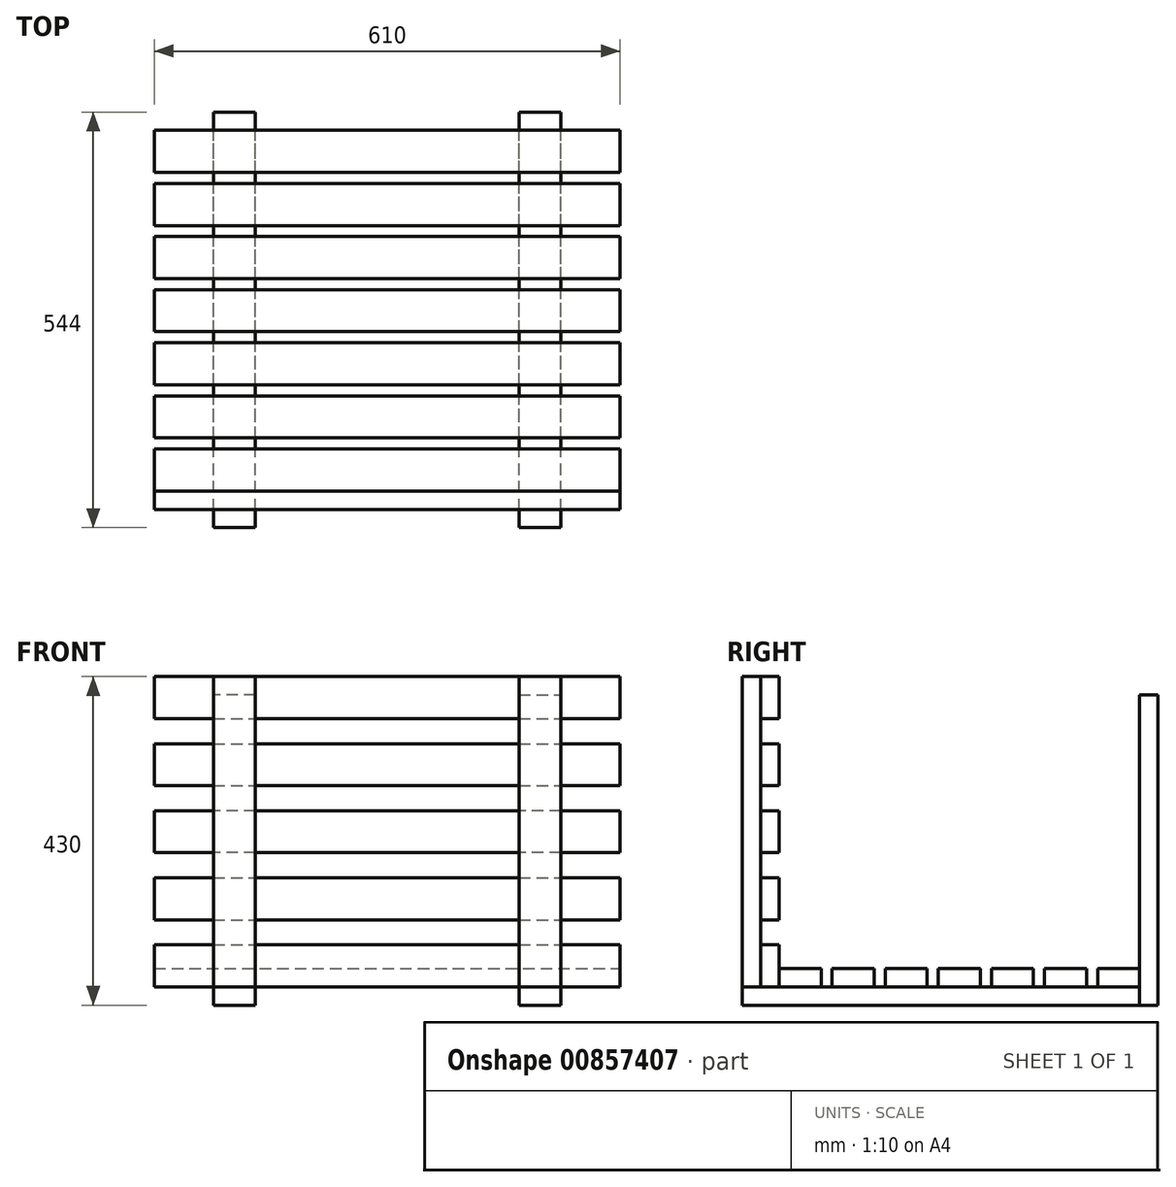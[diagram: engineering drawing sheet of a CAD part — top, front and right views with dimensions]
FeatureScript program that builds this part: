
annotation { "Feature Type Name" : "Feature", "Feature Type Description" : "" }
export const myFeature = defineFeature(function(context is Context, id is Id, definition is map)
    precondition{}
    {
        {
            assignVariable(context, id + "F0", {"name" : "Brettstaerke", "anyValue" : 24});
        }
        {
            assignVariable(context, id + "F1", {"name" : "Verbinderstaerke", "anyValue" : 24});
        }
        {
            var Q0;
            Q0=qCreatedBy(makeId("Front.planeOp"),FACE);
            var sketch = newSketch(context, id + "F2", { "sketchPlane" : qUnion([Q0])});
            skLineSegment(sketch, "E0.bottom", {"start": v(305, 27.5) * mm, "end": v(-305, 27.5) * mm});
            skLineSegment(sketch, "E0.top", {"start": v(305, -27.5) * mm, "end": v(-305, -27.5) * mm});
            skLineSegment(sketch, "E0.left", {"start": v(305, 27.5) * mm, "end": v(305, -27.5) * mm});
            skLineSegment(sketch, "E0.right", {"start": v(-305, 27.5) * mm, "end": v(-305, -27.5) * mm});
            skPoint(sketch, "E0.middle", {"position": v(0, 0) * mm});
            skLineSegment(sketch, "E1.bottom", {"start": v(-305, 115.25) * mm, "end": v(305, 115.25) * mm});
            skLineSegment(sketch, "E1.top", {"start": v(-305, 60.25) * mm, "end": v(305, 60.25) * mm});
            skLineSegment(sketch, "E1.left", {"start": v(-305, 115.25) * mm, "end": v(-305, 60.25) * mm});
            skLineSegment(sketch, "E1.right", {"start": v(305, 115.25) * mm, "end": v(305, 60.25) * mm});
            skLineSegment(sketch, "E2.bottom", {"start": v(-305, 203) * mm, "end": v(305, 203) * mm});
            skLineSegment(sketch, "E2.top", {"start": v(-305, 148) * mm, "end": v(305, 148) * mm});
            skLineSegment(sketch, "E2.left", {"start": v(-305, 203) * mm, "end": v(-305, 148) * mm});
            skLineSegment(sketch, "E2.right", {"start": v(305, 203) * mm, "end": v(305, 148) * mm});
            skLineSegment(sketch, "E3.bottom", {"start": v(-305, -148) * mm, "end": v(305, -148) * mm});
            skLineSegment(sketch, "E3.top", {"start": v(-305, -203) * mm, "end": v(305, -203) * mm});
            skLineSegment(sketch, "E3.left", {"start": v(-305, -148) * mm, "end": v(-305, -203) * mm});
            skLineSegment(sketch, "E3.right", {"start": v(305, -148) * mm, "end": v(305, -203) * mm});
            skLineSegment(sketch, "E4", {"start": v(-305, 27.5) * mm, "end": v(-305, 60.25) * mm, "construction": true});
            skLineSegment(sketch, "E5", {"start": v(-305, 115.25) * mm, "end": v(-305, 148) * mm, "construction": true});
            skLineSegment(sketch, "E6.bottom", {"start": v(-305, -60.25) * mm, "end": v(305, -60.25) * mm});
            skLineSegment(sketch, "E6.top", {"start": v(-305, -115.25) * mm, "end": v(305, -115.25) * mm});
            skLineSegment(sketch, "E6.left", {"start": v(-305, -60.25) * mm, "end": v(-305, -115.25) * mm});
            skLineSegment(sketch, "E6.right", {"start": v(305, -60.25) * mm, "end": v(305, -115.25) * mm});
            skLineSegment(sketch, "E7", {"start": v(-305, -60.25) * mm, "end": v(-305, -27.5) * mm, "construction": true});
            skLineSegment(sketch, "E8", {"start": v(-305, -148) * mm, "end": v(-305, -115.25) * mm, "construction": true});
            skSolve(sketch);
        }
        {
            var Q0;
            Q0=makeQuery(id+"F2.imprint","IMPRINT",FACE,{"disambiguationData":[TD([[makeQuery(id+"F2.imprint","IMPRINT",EDGE,{"derivedFrom":sQuery(id+"F2.wireOp",EDGE,"E2.bottom")}),-1.0]])]});
            var Q1;
            Q1=makeQuery(id+"F2.imprint","IMPRINT",FACE,{"disambiguationData":[TD([[makeQuery(id+"F2.imprint","IMPRINT",EDGE,{"derivedFrom":sQuery(id+"F2.wireOp",EDGE,"E1.bottom")}),-1.0]])]});
            var Q2;
            Q2=makeQuery(id+"F2.imprint","IMPRINT",FACE,{"disambiguationData":[TD([[makeQuery(id+"F2.imprint","IMPRINT",EDGE,{"derivedFrom":sQuery(id+"F2.wireOp",EDGE,"E0.bottom")}),1.0]])]});
            var Q3;
            Q3=makeQuery(id+"F2.imprint","IMPRINT",FACE,{"disambiguationData":[TD([[makeQuery(id+"F2.imprint","IMPRINT",EDGE,{"derivedFrom":sQuery(id+"F2.wireOp",EDGE,"E3.bottom")}),-1.0]])]});
            var Q4;
            Q4=makeQuery(id+"F2.imprint","IMPRINT",FACE,{"disambiguationData":[TD([[makeQuery(id+"F2.imprint","IMPRINT",EDGE,{"derivedFrom":sQuery(id+"F2.wireOp",EDGE,"E6.bottom")}),-1.0]])]});
            extrude(context, id + "F3", {"entities" : qUnion([Q0, Q1, Q2, Q3, Q4]), "depth" : (getVariable(context, 'Brettstaerke')) * mm, "offsetDistance" : 25 * mm});
        }
        {
            var Q0;
            Q0=makeQuery(id+"F3.opExtrude","CAP_FACE",FACE,{"disambiguationData":[OSD([sQuery(id+"F2.wireOp",EDGE,"E2.bottom"),sQuery(id+"F2.wireOp",EDGE,"E2.top"),sQuery(id+"F2.wireOp",EDGE,"E2.left"),sQuery(id+"F2.wireOp",EDGE,"E2.right")])],"isStart":false});
            var sketch = newSketch(context, id + "F4", { "sketchPlane" : qUnion([Q0])});
            skLineSegment(sketch, "E9.bottom", {"start": v(-227.5, 203) * mm, "end": v(-172.5, 203) * mm});
            skLineSegment(sketch, "E9.top", {"start": v(-227.5, -203) * mm, "end": v(-172.5, -203) * mm});
            skLineSegment(sketch, "E9.left", {"start": v(-227.5, 203) * mm, "end": v(-227.5, -203) * mm});
            skLineSegment(sketch, "E9.right", {"start": v(-172.5, 203) * mm, "end": v(-172.5, -203) * mm});
            skLineSegment(sketch, "E10", {"start": v(-200, 203) * mm, "end": v(-200, -203) * mm, "construction": true});
            skLineSegment(sketch, "E11.bottom", {"start": v(172.5, 203) * mm, "end": v(227.5, 203) * mm});
            skLineSegment(sketch, "E11.top", {"start": v(172.5, -203) * mm, "end": v(227.5, -203) * mm});
            skLineSegment(sketch, "E11.left", {"start": v(172.5, 203) * mm, "end": v(172.5, -203) * mm});
            skLineSegment(sketch, "E11.right", {"start": v(227.5, 203) * mm, "end": v(227.5, -203) * mm});
            skLineSegment(sketch, "E12", {"start": v(200, 203) * mm, "end": v(200, -203) * mm, "construction": true});
            skSolve(sketch);
        }
        {
            var Q0;
            Q0 = qSketchRegion(id + "F4", true);
            extrude(context, id + "F5", {"entities" : qUnion([Q0]), "depth" : (getVariable(context, 'Verbinderstaerke')) * mm, "offsetDistance" : 25 * mm});
        }
        {
            var Q0;
            Q0=makeQuery(id+"F5.opExtrude","SWEPT_FACE",FACE,{"disambiguationData":[OSD([sQuery(id+"F4.wireOp",EDGE,"E11.top")])]});
            var sketch = newSketch(context, id + "F6", { "sketchPlane" : qUnion([Q0])});
            skLineSegment(sketch, "E13.bottom", {"start": v(227.5, 48) * mm, "end": v(172.5, 48) * mm});
            skLineSegment(sketch, "E13.top", {"start": v(227.5, -472) * mm, "end": v(172.5, -472) * mm});
            skLineSegment(sketch, "E13.left", {"start": v(227.5, 48) * mm, "end": v(227.5, -472) * mm});
            skLineSegment(sketch, "E13.right", {"start": v(172.5, 48) * mm, "end": v(172.5, -472) * mm});
            skLineSegment(sketch, "E14.bottom", {"start": v(-172.5, 48) * mm, "end": v(-227.5, 48) * mm});
            skLineSegment(sketch, "E14.top", {"start": v(-172.5, -472) * mm, "end": v(-227.5, -472) * mm});
            skLineSegment(sketch, "E14.left", {"start": v(-172.5, 48) * mm, "end": v(-172.5, -472) * mm});
            skLineSegment(sketch, "E14.right", {"start": v(-227.5, 48) * mm, "end": v(-227.5, -472) * mm});
            skSolve(sketch);
        }
        {
            var Q0;
            {var subQ0=sQuery(id+"F6.wireOp",EDGE,"E13.top");Q0=makeQuery(id+"F6.imprint","IMPRINT",FACE,{"disambiguationData":[TD([[makeQuery(id+"F6.imprint","IMPRINT",EDGE,{"derivedFrom":subQ0}),-1.0]])]});}
            var Q1;
            Q1=makeQuery(id+"F6.imprint","IMPRINT",FACE,{"disambiguationData":[TD([[makeQuery(id+"F6.imprint","IMPRINT",EDGE,{"derivedFrom":sQuery(id+"F6.wireOp",EDGE,"E14.bottom")}),1.0]])]});
            var Q2;
            {var subQ0=sQuery(id+"F6.wireOp",EDGE,"E13.bottom");Q2=makeQuery(id+"F6.imprint","IMPRINT",FACE,{"disambiguationData":[TD([[makeQuery(id+"F6.imprint","IMPRINT",EDGE,{"derivedFrom":subQ0}),-1.0]])]});}
            extrude(context, id + "F7", {"entities" : qUnion([Q0, Q1, Q2]), "depth" : (getVariable(context, 'Verbinderstaerke')) * mm, "offsetDistance" : 25 * mm});
        }
        {
            var Q0;
            Q0=makeQuery(id+"F7.opExtrude","SWEPT_FACE",FACE,{"disambiguationData":[OSD([sQuery(id+"F6.wireOp",EDGE,"E13.top")])]});
            var sketch = newSketch(context, id + "F8", { "sketchPlane" : qUnion([Q0])});
            skLineSegment(sketch, "E15.bottom", {"start": v(-172.5, -227) * mm, "end": v(-227.5, -227) * mm});
            skLineSegment(sketch, "E15.top", {"start": v(-172.5, 179) * mm, "end": v(-227.5, 179) * mm});
            skLineSegment(sketch, "E15.left", {"start": v(-172.5, -227) * mm, "end": v(-172.5, 179) * mm});
            skLineSegment(sketch, "E15.right", {"start": v(-227.5, -227) * mm, "end": v(-227.5, 179) * mm});
            skLineSegment(sketch, "E16.bottom", {"start": v(172.5, -227) * mm, "end": v(227.5, -227) * mm});
            skLineSegment(sketch, "E16.top", {"start": v(172.5, 179) * mm, "end": v(227.5, 179) * mm});
            skLineSegment(sketch, "E16.left", {"start": v(172.5, -227) * mm, "end": v(172.5, 179) * mm});
            skLineSegment(sketch, "E16.right", {"start": v(227.5, -227) * mm, "end": v(227.5, 179) * mm});
            skSolve(sketch);
        }
        {
            var Q0;
            Q0 = qSketchRegion(id + "F8", true);
            extrude(context, id + "F9", {"entities" : qUnion([Q0]), "depth" : (getVariable(context, 'Brettstaerke')) * mm, "offsetDistance" : 25 * mm});
        }
        {
            var Q0;
            Q0=makeQuery(id+"F7.opExtrude","CAP_FACE",FACE,{"disambiguationData":[OSD([sQuery(id+"F6.wireOp",EDGE,"E13.bottom"),sQuery(id+"F6.wireOp",EDGE,"E13.top"),sQuery(id+"F6.wireOp",EDGE,"E13.left"),sQuery(id+"F6.wireOp",EDGE,"E13.right")])],"isStart":true});
            var sketch = newSketch(context, id + "F10", { "sketchPlane" : qUnion([Q0])});
            skLineSegment(sketch, "E17.bottom", {"start": v(305, 0) * mm, "end": v(-305, 0) * mm});
            skLineSegment(sketch, "E17.top", {"start": v(305, 55) * mm, "end": v(-305, 55) * mm});
            skLineSegment(sketch, "E17.left", {"start": v(305, 0) * mm, "end": v(305, 55) * mm});
            skLineSegment(sketch, "E17.right", {"start": v(-305, 0) * mm, "end": v(-305, 55) * mm});
            skLineSegment(sketch, "E18.bottom", {"start": v(-305, 124.5) * mm, "end": v(305, 124.5) * mm});
            skLineSegment(sketch, "E18.top", {"start": v(-305, 69.5) * mm, "end": v(305, 69.5) * mm});
            skLineSegment(sketch, "E18.left", {"start": v(-305, 124.5) * mm, "end": v(-305, 69.5) * mm});
            skLineSegment(sketch, "E18.right", {"start": v(305, 124.5) * mm, "end": v(305, 69.5) * mm});
            skLineSegment(sketch, "E19.bottom", {"start": v(-305, 194) * mm, "end": v(305, 194) * mm});
            skLineSegment(sketch, "E19.top", {"start": v(-305, 139) * mm, "end": v(305, 139) * mm});
            skLineSegment(sketch, "E19.left", {"start": v(-305, 194) * mm, "end": v(-305, 139) * mm});
            skLineSegment(sketch, "E19.right", {"start": v(305, 194) * mm, "end": v(305, 139) * mm});
            skLineSegment(sketch, "E20.bottom", {"start": v(-305, 263.5) * mm, "end": v(305, 263.5) * mm});
            skLineSegment(sketch, "E20.top", {"start": v(-305, 208.5) * mm, "end": v(305, 208.5) * mm});
            skLineSegment(sketch, "E20.left", {"start": v(-305, 263.5) * mm, "end": v(-305, 208.5) * mm});
            skLineSegment(sketch, "E20.right", {"start": v(305, 263.5) * mm, "end": v(305, 208.5) * mm});
            skLineSegment(sketch, "E21.bottom", {"start": v(-305, 333) * mm, "end": v(305, 333) * mm});
            skLineSegment(sketch, "E21.top", {"start": v(-305, 278) * mm, "end": v(305, 278) * mm});
            skLineSegment(sketch, "E21.left", {"start": v(-305, 333) * mm, "end": v(-305, 278) * mm});
            skLineSegment(sketch, "E21.right", {"start": v(305, 333) * mm, "end": v(305, 278) * mm});
            skLineSegment(sketch, "E22.bottom", {"start": v(-305, 402.5) * mm, "end": v(305, 402.5) * mm});
            skLineSegment(sketch, "E22.top", {"start": v(-305, 347.5) * mm, "end": v(305, 347.5) * mm});
            skLineSegment(sketch, "E22.left", {"start": v(-305, 402.5) * mm, "end": v(-305, 347.5) * mm});
            skLineSegment(sketch, "E22.right", {"start": v(305, 402.5) * mm, "end": v(305, 347.5) * mm});
            skLineSegment(sketch, "E23.bottom", {"start": v(-305, 472) * mm, "end": v(305, 472) * mm});
            skLineSegment(sketch, "E23.top", {"start": v(-305, 417) * mm, "end": v(305, 417) * mm});
            skLineSegment(sketch, "E23.left", {"start": v(-305, 472) * mm, "end": v(-305, 417) * mm});
            skLineSegment(sketch, "E23.right", {"start": v(305, 472) * mm, "end": v(305, 417) * mm});
            skLineSegment(sketch, "E24", {"start": v(-305, 55) * mm, "end": v(-305, 69.5) * mm, "construction": true});
            skLineSegment(sketch, "E25", {"start": v(-305, 124.5) * mm, "end": v(-305, 139) * mm, "construction": true});
            skLineSegment(sketch, "E26", {"start": v(-305, 194) * mm, "end": v(-305, 208.5) * mm, "construction": true});
            skLineSegment(sketch, "E27", {"start": v(-305, 263.5) * mm, "end": v(-305, 278) * mm, "construction": true});
            skLineSegment(sketch, "E28", {"start": v(-305, 333) * mm, "end": v(-305, 347.5) * mm, "construction": true});
            skLineSegment(sketch, "E29", {"start": v(-305, 402.5) * mm, "end": v(-305, 417) * mm, "construction": true});
            skSolve(sketch);
        }
        {
            var Q0;
            Q0 = qSketchRegion(id + "F10", true);
            extrude(context, id + "F11", {"entities" : qUnion([Q0]), "depth" : (getVariable(context, 'Brettstaerke')) * mm, "offsetDistance" : 25 * mm});
        }
    });
